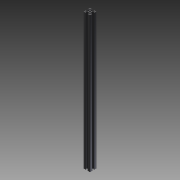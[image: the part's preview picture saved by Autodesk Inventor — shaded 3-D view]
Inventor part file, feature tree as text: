
AUTODESK INVENTOR PART (.ipt)
format: ipt  version: 2014 SP1 (Build 180222100, 222)  size: 177,152 bytes
history: native  units: mm
features: other x7, sketch x2, extrude x1, revolve x1
ambient origin geometry x8: Origin, YZ Plane, XZ Plane, XY Plane, X Axis, Y Axis, Z Axis, Center Point
bodies: Solid1 (feature_tree)
feature tree (11):
  extrude  "Extrusion1"  TaperAngle=360.0deg  [1 undecoded]
  revolve  "Revolution1"  [1 undecoded]
  other  "C1_XY"
  other  "C1_YZ"
  other  "C1_ZX"
  other  "C1_X"
  other  "C1_Y"
  other  "C1_Z"
  other  "C1_Center"
  sketch  "Sketch_1"  dims[d0=425.0mm d1=0.0mm d2=360.0deg]
  sketch  "Sketch_2"
note: 2 required parameter values undecoded (feature->parameter linkage not recoverable at this tier; creation-order binding heuristic only, values carry confidence <= 0.55)
